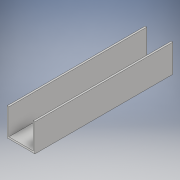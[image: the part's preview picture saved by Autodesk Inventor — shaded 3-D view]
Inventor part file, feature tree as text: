
AUTODESK INVENTOR PART (.ipt)
format: ipt  version: 2017 (Build 210142000, 142)  size: 98,816 bytes
history: native  units: in
note: dims shown in document units (in); Inventor stores cm internally (conversion verified against a paired STEP export)
features: sketch x2, extrude x1
ambient origin geometry x8: Origin, YZ Plane, XZ Plane, XY Plane, X Axis, Y Axis, Z Axis, Center Point
bodies: Solid1 (feature_tree)
feature tree (3):
  sketch  "Sketch1"  dims[d2=0.079in d3=1.26in]
  sketch  "Sketch2"  dims[d5=6.25in d6=0.0in]
  extrude  "Extrusion1"  Depth=1.26in
